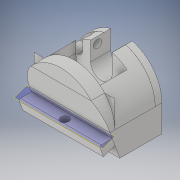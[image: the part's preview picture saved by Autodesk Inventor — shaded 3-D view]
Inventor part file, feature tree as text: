
AUTODESK INVENTOR PART (.ipt)
format: ipt  version: 2018 (Build 220112000, 112)  size: 276,480 bytes
history: native  units: in
note: dims shown in document units (in); Inventor stores cm internally (conversion verified against a paired STEP export)
features: extrude x11, sketch x11, plane x1, fillet x1
ambient origin geometry x8: Origin, YZ Plane, XZ Plane, XY Plane, X Axis, Y Axis, Z Axis, Center Point
bodies: Solid1 (feature_tree)
feature tree (24):
  extrude  "Extrusion1"  Depth=0.5906in
  sketch  "Sketch2"  dims[d2=0.1969in d3=0.0in d10=0.1969in]
  extrude  "Extrusion3"  Depth=0.1969in
  extrude  "Extrusion4"  Depth=0.5906in TaperAngle=0.0deg
  extrude  "Extrusion5"  Depth=0.374in
  extrude  "Extrusion6"  Depth=0.3937in TaperAngle=0.0deg
  extrude  "Extrusion8"  Depth=0.1181in
  plane  "Work Plane3"
  extrude  "Extrusion10"  Depth=0.1969in TaperAngle=0.0deg
  extrude  "Extrusion11"  Depth=0.0236in
  extrude  "Extrusion12"  Depth=0.1969in
  extrude  "Extrusion13"  Depth=0.1772in
  fillet  "Fillet1"  Radius=0.1772in
  extrude  "Extrusion14"  Depth=0.0197in
  sketch  "Sketch1"  dims[d0=1.1811in d1=0.5906in]
  sketch  "Sketch3"  dims[d11=1.1811in d12=0.5906in d13=0.0in]
  sketch  "Sketch4"  dims[d14=0.2953in d15=0.374in]
  sketch  "Sketch5"  dims[d19=0.374in d20=0.3937in d21=0.0in]
  sketch  "Sketch6"  dims[d22=0.315in d23=0.1181in]
  sketch  "Sketch10"  dims[d24=0.0787in d25=0.1969in d26=0.0in]
  sketch  "Sketch12"  dims[d27=0.315in d28=0.0236in]
  sketch  "Sketch13"  dims[d29=0.1181in d30=0.0in d37=0.1969in]
  sketch  "Sketch14"  dims[d38=1.1811in d39=0.0in d46=0.1181in d48=0.1772in]
  sketch  "Sketch15"  dims[d50=-0.1772in d51=0.0197in d52=0.5906in d53=0.0984in d54=0.1181in d55=0.2756in d56=0.0in d57=0.3937in d58=0.1969in d59=1.1811in d60=0.0in d61=0.1969in d62=0.0in d63=0.7559in d64=1.1811in d65=0.0in d66=0.0197in d67=0.0984in d68=0.0in d69=0.1181in]
